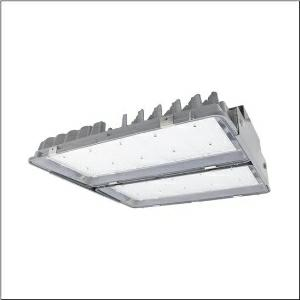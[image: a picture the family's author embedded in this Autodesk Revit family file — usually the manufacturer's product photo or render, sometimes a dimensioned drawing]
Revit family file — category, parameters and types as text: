
# Revit family: highbay_11xtreme_51hf82db4wma
name_source: partatom
category: Lighting Fixtures
units: mm (PartAtom-declared; Revit-internal decimal feet)

## family parameters
Cut with Voids When Loaded = No
Host = Face
Light Source = No
Part Type = Normal
Room Calculation Point = No
Round Connector Dimension = Use Diameter
Shared = No

## types (1)
- --- (1 x LED, 75000 lm, 422.2 W, 4000K)
    Apparent Load = 422 VA
    CIE Flux Codes = 84 96 100 100 100
    Color Rendering = 80
    Color Temperature = 4000K
    Default Elevation = 1800 mm
    Description = Highbay 11Xtreme, high bay luminaire, primary light control with lens, of PMMA, primary optical cover: cover, of toughened safety glass, light emission: direct distribution, primary light characteristic: symmetric, installation type: suspended mounting, surface-mounted, 2x LED module,for 1x 2x LED, rated luminous flux: 75.000lm, luminous efficacy: 178lm/W, light colour: 840, colour temperature: 4000K, control gear: DALI 2 (with two DALI addresses), with cable H07RN-F 5x 1.5mm², mains connection: 220..240V, AC, 50/60Hz, cable length: 1,5m, rated input power: 422W, luminaire housing, of diecast aluminium, partly coated, silver, length: 595mm, width: 560mm, height: 195mm, protection rating (complete): IP66, insulation class (complete): insulation class I (protective earthing), certification: CE, ENEC, UKCA, protection symbol: D, ball protection: ball impact resistant according to DIN VDE 0710 part 13 (with chain suspension), impact resistance: IK08, permissible operating ambient temperature: -25..+45°C, reducing of maximum allowable ambient temperature of 5°C with ceiling mounting, packaging unit: 1 piece
    Height = 157 mm
    Lamp = 1 x LED
    Lamp Light Flux = 75000 lm
    Lamp Power = 422.2 W
    Lamp count = 1
    Length = 593 mm
    Luminous efficacy = 178 lm/W
    Manufacturer = Siteco
    ModVariant = No
    Model = 51HF82DB4WMA
    Mounting Place = Ceiling
    Mounting Type = Pendant
    Number of Poles = 1
    OnlyDefault = Yes
    Power Factor = 1
    Product Name = Highbay 11Xtreme
    Product group = high bay luminaire
    ProductGroupID = 902
    Protection Class = Protection class I
    Protection Degree = IP 66
    RLX_Detail_Level = 1
    RLX_Emergency_Light_Flux = 0 lm
    RLX_Emergency_Type = 0
    RLX_Emergency_Type_DB = No
    RlxData = <blob elided: 34365 chars, md5=bd6d0c2a>
    Socket = socket
    Standby Power = 0 W
    System Light Flux = 75000 lm
    System Power = 422 W
    Type Comments = factory setting: luminous flux: 100 % | dim-lin: 254 | 1389 mA
    Type Image = l_1258340.jpg
    URL = http://relux.com
    VarID = @adj_088239
    Voltage = 0 V
    Weight = 0.00 kg
    Width = 568 mm

## geometry (parser evidence)
native form markers: Blend x4, Sweep x9
no freeform markers — native parametric forms only
